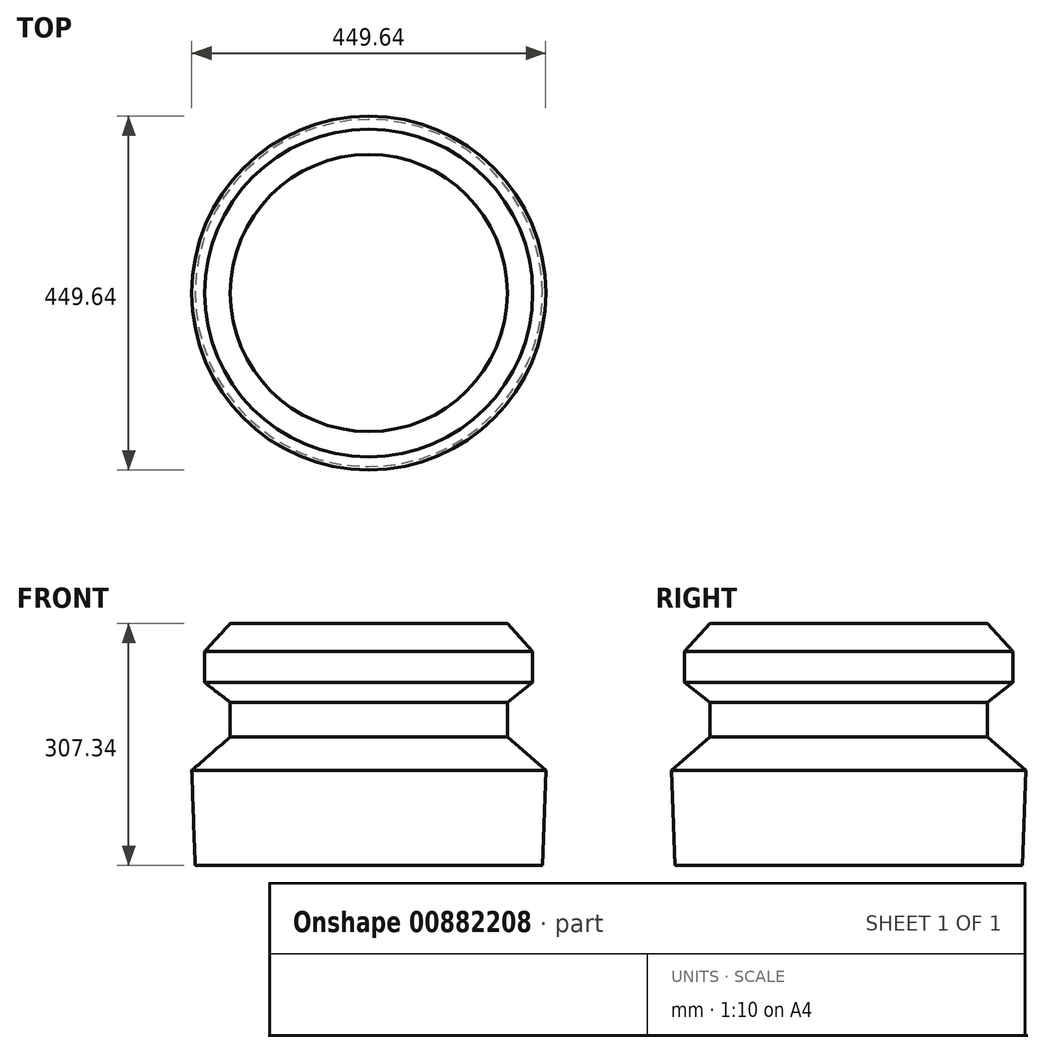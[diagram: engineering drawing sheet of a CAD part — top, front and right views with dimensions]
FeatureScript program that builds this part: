
annotation { "Feature Type Name" : "Feature", "Feature Type Description" : "" }
export const myFeature = defineFeature(function(context is Context, id is Id, definition is map)
    precondition{}
    {
        {
            var Q0;
            Q0=qCreatedBy(makeId("Right.planeOp"),FACE);
            var sketch = newSketch(context, id + "F0", { "sketchPlane" : qUnion([Q0])});
            skLineSegment(sketch, "E0", {"start": v(0, 0) * mm, "end": v(0, 307.34) * mm});
            skLineSegment(sketch, "E1", {"start": v(0, 307.34) * mm, "end": v(-176, 307.34) * mm});
            skLineSegment(sketch, "E2", {"start": v(-176, 307.34) * mm, "end": v(-208.35, 271.93) * mm});
            skLineSegment(sketch, "E3", {"start": v(-208.35, 271.93) * mm, "end": v(-208.35, 232.26) * mm});
            skLineSegment(sketch, "E4", {"start": v(-208.35, 232.26) * mm, "end": v(-176, 207.23) * mm});
            skLineSegment(sketch, "E5", {"start": v(-176, 207.23) * mm, "end": v(-176, 163.28) * mm});
            skLineSegment(sketch, "E6", {"start": v(-176, 163.28) * mm, "end": v(-224.82, 120.55) * mm});
            skLineSegment(sketch, "E7", {"start": v(-224.82, 120.55) * mm, "end": v(-220.55, 0) * mm});
            skLineSegment(sketch, "E8", {"start": v(-220.55, 0) * mm, "end": v(0, 0) * mm});
            skSolve(sketch);
        }
        {
            var Q0;
            Q0=makeQuery(id+"F0.imprint","IMPRINT",FACE,{"disambiguationData":[TD([[makeQuery(id+"F0.imprint","IMPRINT",EDGE,{"derivedFrom":sQuery(id+"F0.wireOp",EDGE,"E0")}),1.0]])]});
            var Q1;
            Q1=sQuery(id+"F0.wireOp",EDGE,"E0");
            revolve(context, id + "F1", {"surfaceOperationType" : NewSurfaceOperationType.NEW, "entities" : qUnion([Q0]), "axis" : qUnion([Q1]), "revolveType" : RevolveType.FULL});
        }
    });
